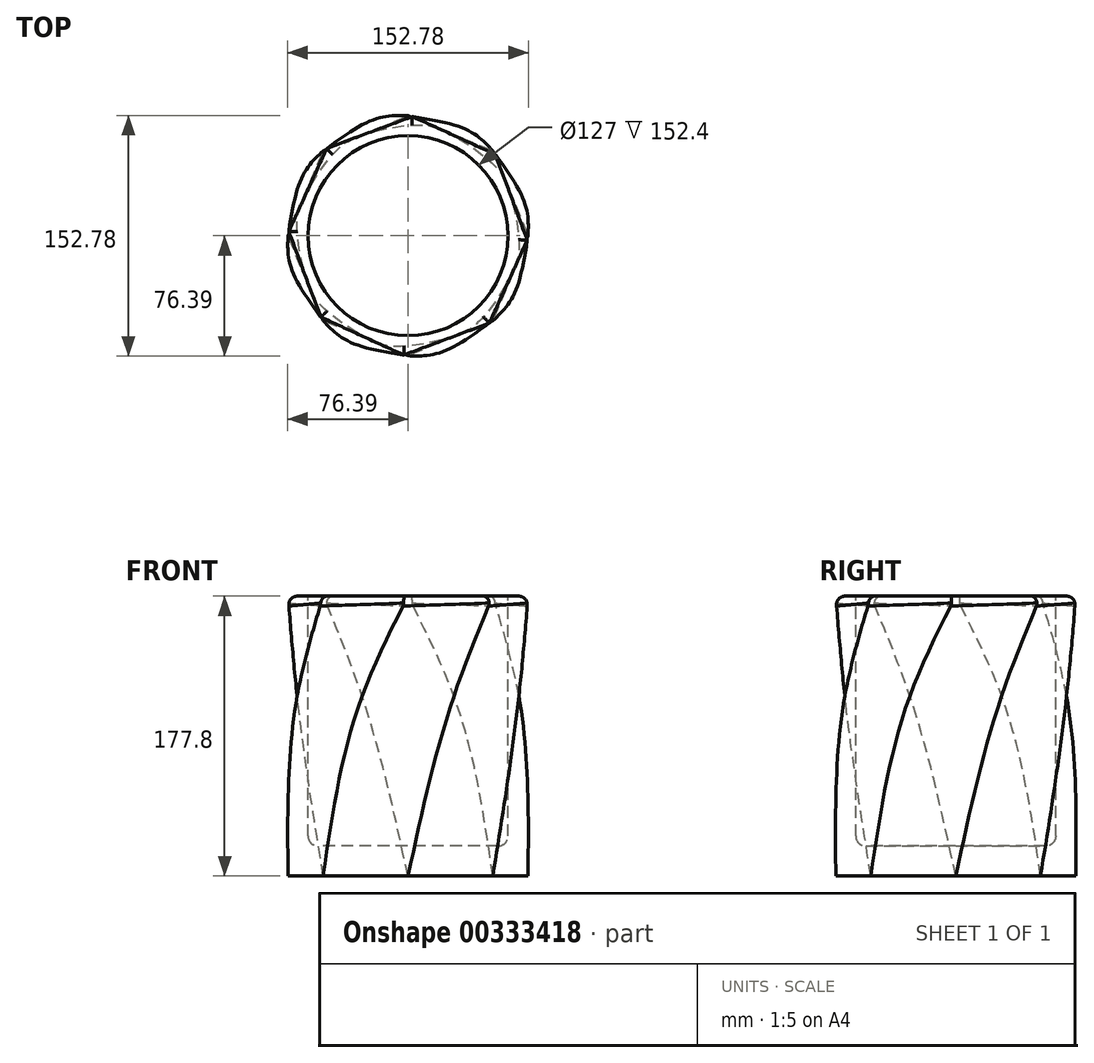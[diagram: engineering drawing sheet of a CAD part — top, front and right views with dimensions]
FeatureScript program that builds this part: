
annotation { "Feature Type Name" : "Feature", "Feature Type Description" : "" }
export const myFeature = defineFeature(function(context is Context, id is Id, definition is map)
    precondition{}
    {
        {
            var Q0;
            Q0=qCreatedBy(makeId("Top.planeOp"),FACE);
            var sketch = newSketch(context, id + "F0", { "sketchPlane" : qUnion([Q0])});
            skCircle(sketch, "E0.cCircle", {"center": v(0, 0) * mm, "radius": 70.4 * mm, "construction": true});
            skLineSegment(sketch, "E0.0", {"start": v(53.88, 53.88) * mm, "end": v(76.2, 0) * mm});
            skLineSegment(sketch, "E0.1", {"start": v(76.2, 0) * mm, "end": v(53.88, -53.88) * mm});
            skLineSegment(sketch, "E0.2", {"start": v(53.88, -53.88) * mm, "end": v(0, -76.2) * mm});
            skLineSegment(sketch, "E0.3", {"start": v(0, -76.2) * mm, "end": v(-53.88, -53.88) * mm});
            skLineSegment(sketch, "E0.4", {"start": v(-53.88, -53.88) * mm, "end": v(-76.2, 0) * mm});
            skLineSegment(sketch, "E0.5", {"start": v(-76.2, 0) * mm, "end": v(-53.88, 53.88) * mm});
            skLineSegment(sketch, "E0.6", {"start": v(-53.88, 53.88) * mm, "end": v(0, 76.2) * mm});
            skLineSegment(sketch, "E0.7", {"start": v(0, 76.2) * mm, "end": v(53.88, 53.88) * mm});
            skPoint(sketch, "E0.0.midPoint", {"position": v(65.04, 26.94) * mm});
            skSolve(sketch);
        }
        {
            var Q0;
            Q0=qCreatedBy(makeId("Top.planeOp"),FACE);
            cPlane(context, id + "F1", {"entities" : qUnion([Q0]), "cplaneType" : CPlaneType.OFFSET, "offset" : 114.3 * mm, "width" : 152.4 * mm, "height" : 152.4 * mm});
        }
        {
            var Q0;
            Q0=qCreatedBy(id+"F1.planeOp",FACE);
            cPlane(context, id + "F2", {"entities" : qUnion([Q0]), "cplaneType" : CPlaneType.OFFSET, "offset" : 63.5 * mm, "width" : 152.4 * mm, "height" : 152.4 * mm});
        }
        {
            var Q0;
            Q0=qCreatedBy(id+"F1.planeOp",FACE);
            var sketch = newSketch(context, id + "F3", { "sketchPlane" : qUnion([Q0])});
            skCircle(sketch, "E1.cCircle", {"center": v(0, 0) * mm, "radius": 70.4 * mm, "construction": true});
            skLineSegment(sketch, "E1.0", {"start": v(70.4, 29.16) * mm, "end": v(70.4, -29.16) * mm});
            skLineSegment(sketch, "E1.1", {"start": v(70.4, -29.16) * mm, "end": v(29.16, -70.4) * mm});
            skLineSegment(sketch, "E1.2", {"start": v(29.16, -70.4) * mm, "end": v(-29.16, -70.4) * mm});
            skLineSegment(sketch, "E1.3", {"start": v(-29.16, -70.4) * mm, "end": v(-70.4, -29.16) * mm});
            skLineSegment(sketch, "E1.4", {"start": v(-70.4, -29.16) * mm, "end": v(-70.4, 29.16) * mm});
            skLineSegment(sketch, "E1.5", {"start": v(-70.4, 29.16) * mm, "end": v(-29.16, 70.4) * mm});
            skLineSegment(sketch, "E1.6", {"start": v(-29.16, 70.4) * mm, "end": v(29.16, 70.4) * mm});
            skLineSegment(sketch, "E1.7", {"start": v(29.16, 70.4) * mm, "end": v(70.4, 29.16) * mm});
            skPoint(sketch, "E1.0.midPoint", {"position": v(70.4, 0) * mm});
            skSolve(sketch);
        }
        {
            var Q0;
            Q0=qCreatedBy(id+"F2.planeOp",FACE);
            var sketch = newSketch(context, id + "F4", { "sketchPlane" : qUnion([Q0])});
            skCircle(sketch, "E2.cCircle", {"center": v(0, 0) * mm, "radius": 70.4 * mm, "construction": true});
            skLineSegment(sketch, "E2.0", {"start": v(53.88, 53.88) * mm, "end": v(76.2, 0) * mm});
            skLineSegment(sketch, "E2.1", {"start": v(76.2, 0) * mm, "end": v(53.88, -53.88) * mm});
            skLineSegment(sketch, "E2.2", {"start": v(53.88, -53.88) * mm, "end": v(0, -76.2) * mm});
            skLineSegment(sketch, "E2.3", {"start": v(0, -76.2) * mm, "end": v(-53.88, -53.88) * mm});
            skLineSegment(sketch, "E2.4", {"start": v(-53.88, -53.88) * mm, "end": v(-76.2, 0) * mm});
            skLineSegment(sketch, "E2.5", {"start": v(-76.2, 0) * mm, "end": v(-53.88, 53.88) * mm});
            skLineSegment(sketch, "E2.6", {"start": v(-53.88, 53.88) * mm, "end": v(0, 76.2) * mm});
            skLineSegment(sketch, "E2.7", {"start": v(0, 76.2) * mm, "end": v(53.88, 53.88) * mm});
            skPoint(sketch, "E2.0.midPoint", {"position": v(65.04, 26.94) * mm});
            skSolve(sketch);
        }
        {
            var Q0;
            Q0=makeQuery(id+"F0.imprint","IMPRINT",FACE,{"disambiguationData":[TD([[makeQuery(id+"F0.imprint","IMPRINT",EDGE,{"derivedFrom":sQuery(id+"F0.wireOp",EDGE,"E0.0")}),-1.0]])]});
            var Q1;
            Q1=makeQuery(id+"F3.imprint","IMPRINT",FACE,{"disambiguationData":[TD([[makeQuery(id+"F3.imprint","IMPRINT",EDGE,{"derivedFrom":sQuery(id+"F3.wireOp",EDGE,"E1.0")}),-1.0]])]});
            var Q2;
            Q2=makeQuery(id+"F4.imprint","IMPRINT",FACE,{"disambiguationData":[TD([[makeQuery(id+"F4.imprint","IMPRINT",EDGE,{"derivedFrom":sQuery(id+"F4.wireOp",EDGE,"E2.0")}),-1.0]])]});
            var Q3;
            Q3=sQuery(id+"F0.wireOp",VERTEX,"E0.4.start");
            var Q4;
            Q4=sQuery(id+"F3.wireOp",VERTEX,"E1.3.start");
            var Q5;
            Q5=sQuery(id+"F4.wireOp",VERTEX,"E2.3.start");
            loft(context, id + "F5", {"sheetProfilesArray" : [{ "sheetProfileEntities" : qUnion([Q0]) }, { "sheetProfileEntities" : qUnion([Q1]) }, { "sheetProfileEntities" : qUnion([Q2]) }], "matchConnections" : true, "connections" : [{ "connectionEntities" : qUnion([Q3, Q4, Q5]), "connectionEdgeQueries" : qUnion([]), "connectionEdgeParameters" : [] }]});
        }
        {
            var Q0;
            Q0=makeQuery(id+"F5.opLoft","CAP_FACE",FACE,{"disambiguationData":[OSD([makeQuery(id+"F4.imprint","IMPRINT",FACE,{"disambiguationData":[TD([[makeQuery(id+"F4.imprint","IMPRINT",EDGE,{"derivedFrom":sQuery(id+"F4.wireOp",EDGE,"E2.0")}),-1.0]])]})])],"isStart":true});
            fillet(context, id + "F6", {"entities" : qUnion([Q0]), "radius" : 5.08 * mm, "tangentPropagation" : true, "allowEdgeOverflow" : false});
        }
        {
            var Q0;
            Q0=qCreatedBy(id+"F2.planeOp",FACE);
            var sketch = newSketch(context, id + "F7", { "sketchPlane" : qUnion([Q0])});
            skCircle(sketch, "E3", {"center": v(0, 0) * mm, "radius": 63.5 * mm});
            skSolve(sketch);
        }
        {
            var Q0;
            Q0 = qSketchRegion(id + "F7", true);
            extrude(context, id + "F8", {"entities" : qUnion([Q0]), "operationType" : NewBodyOperationType.REMOVE, "oppositeDirection" : true, "depth" : 158.75 * mm});
        }
        {
            var Q0;
            Q0=makeQuery(id+"F8.boolean.opBoolean","COPY",EDGE,{"derivedFrom":makeQuery(id+"F8.opExtrude","CAP_EDGE",EDGE,{"disambiguationData":[OSD([sQuery(id+"F7.wireOp",EDGE,"E3")])],"isStart":false})});
            fillet(context, id + "F9", {"entities" : qUnion([Q0]), "radius" : 6.35 * mm, "tangentPropagation" : true, "allowEdgeOverflow" : false});
        }
    });
